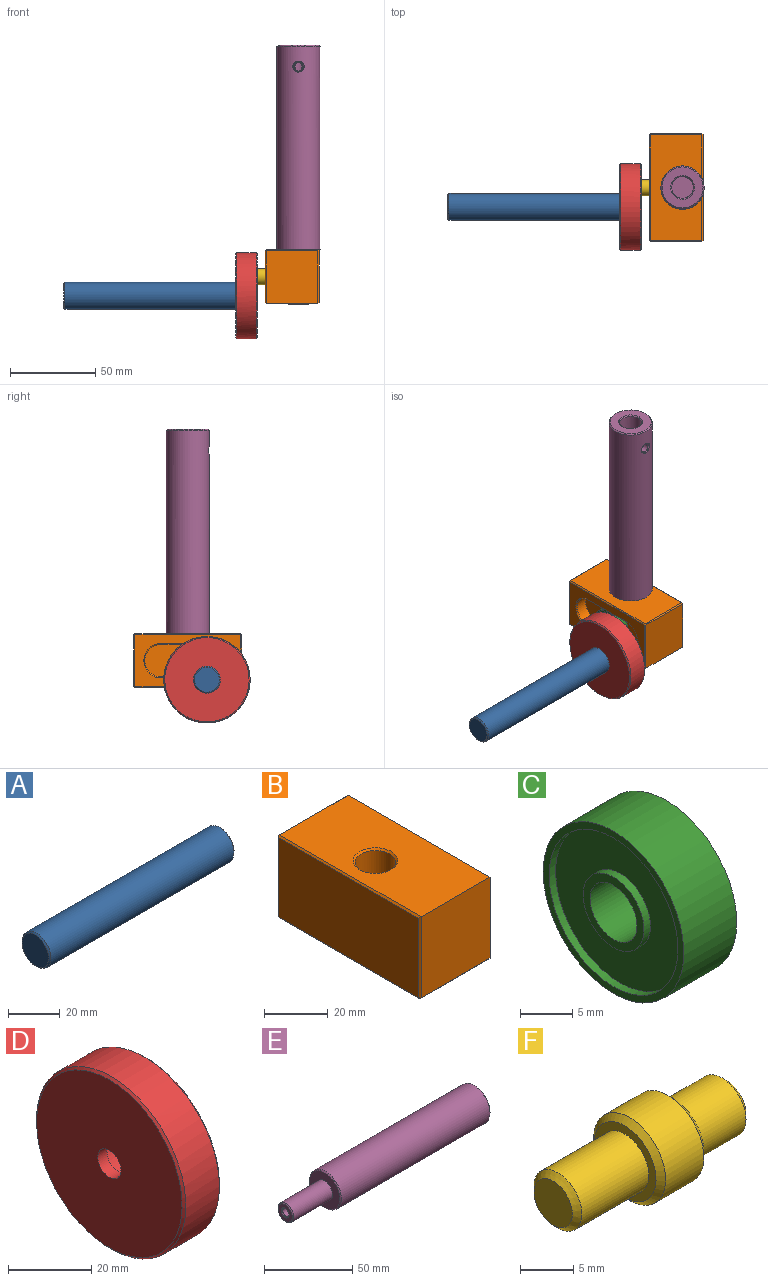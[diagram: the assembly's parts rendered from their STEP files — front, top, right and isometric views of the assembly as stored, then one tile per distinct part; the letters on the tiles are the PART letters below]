
ASSEMBLY  parts=6 mates=5
PART A: 8 faces, bbox 101.6x15.9x15.9 mm
  f0: plane 14.61x14.61mm, normal (-1,0,0), area 167.5mm2, adj f5
  f1: cylinder r=7.94mm len=100.33mm, axis (-1,0,0), area 5003.7mm2, adj f5,f6
  f2: plane 14.61x14.61mm, normal (1,0,0), area 135.6mm2, adj f6,f7
  f3: cone r=0mm half-angle=59deg, axis (1,0,0), area 23.9mm2, adj f4
  f4: cylinder r=2.55mm len=24.77mm, axis (1,0,0), area 397.2mm2, adj f3,f7
  f5: cone r=7.3mm half-angle=45deg, axis (1,0,0), area 43mm2, adj f0,f1
  f6: cone r=7.94mm half-angle=45deg, axis (-1,0,0), area 43mm2, adj f1,f2
  f7: cone r=2.55mm half-angle=45deg, axis (1,0,0), area 16.2mm2, adj f2,f4
PART B: 35 faces, bbox 31.8x63.5x31.8 mm
  f0: plane 62.23x30.48mm, normal (1,0,0), area 933.7mm2, adj f12,f13,f14,f15,f18,f20,f21,f22
  f1: plane 62.87x30.48mm, normal (0,0,1), area 1762.8mm2, adj f2,f17,f18,f23,f24
  f2: plane 31.12x30.48mm, normal (0,-1,0), area 948.4mm2, adj f1,f20,f28,f29
  f3: plane 62.23x30.48mm, normal (0,0,-1), area 1743.5mm2, adj f16,f21,f29,f30,f34
  f4: plane 30.48x30.48mm, normal (0,1,0), area 929mm2, adj f22,f23,f30,f31
  f5: plane 62.23x30.48mm, normal (-1,0,0), area 1896.8mm2, adj f24,f28,f31,f34
  f6: plane 31.75x6.99mm, normal (0,0,-1), area 221.8mm2, adj f7,f9,f10,f13
  f7: cylinder r=9.53mm len=19.05mm, axis (1,0,0), area 206.7mm2, adj f6,f8,f10,f15
  f8: plane 31.75x6.99mm, normal (0,0,1), area 221.8mm2, adj f7,f9,f10,f14
  f9: cylinder r=9.53mm len=19.05mm, axis (1,0,0), area 207mm2, adj f6,f8,f10,f12
  f10: plane 50.48x19.05mm, normal (1,0,0), area 883.9mm2, adj f6,f7,f8,f9
  f11: cylinder r=6.35mm len=30.48mm, axis (0,0,1), area 1216.1mm2, adj f16,f17
  f12: cone r=9.53mm half-angle=45deg, axis (1,0,0), area 27.5mm2, adj f0,f9,f13,f14
  f13: plane 31.76x0.64mm, normal (0.71,0,-0.71), area 28.5mm2, adj f0,f6,f12,f15
  f14: plane 31.76x0.64mm, normal (0.71,0,0.71), area 28.5mm2, adj f0,f8,f12,f15
  f15: cone r=9.53mm half-angle=45deg, axis (1,0,0), area 27.5mm2, adj f0,f7,f13,f14
  f16: cone r=6.99mm half-angle=45deg, axis (0,0,-1), area 37.6mm2, adj f3,f11
  f17: cone r=6.35mm half-angle=45deg, axis (0,0,1), area 37.6mm2, adj f1,f11
  f18: plane 62.87x0.64mm, normal (0.71,0,0.71), area 56.2mm2, adj f0,f1,f19,f20
  f19: plane 0.64x0.64mm, normal (0.58,0.58,0.58), area 0.3mm2, adj f18,f22,f23
  f20: plane 31.12x0.64mm, normal (0.71,-0.71,0), area 27.7mm2, adj f0,f2,f18,f25
  f21: plane 62.23x0.64mm, normal (0.71,0,-0.71), area 55.9mm2, adj f0,f3,f25,f26
  f22: plane 30.48x0.64mm, normal (0.71,0.71,0), area 27.4mm2, adj f0,f4,f19,f26
  f23: plane 30.48x0.64mm, normal (0,0.71,0.71), area 27.4mm2, adj f1,f4,f19,f27
  f24: plane 62.87x0.64mm, normal (-0.71,0,0.71), area 56.2mm2, adj f1,f5,f27,f28
  f25: plane 0.64x0.64mm, normal (0.58,-0.58,-0.58), area 0.3mm2, adj f20,f21,f29
  f26: plane 0.64x0.64mm, normal (0.58,0.58,-0.58), area 0.3mm2, adj f21,f22,f30
  f27: plane 0.64x0.64mm, normal (-0.58,0.58,0.58), area 0.3mm2, adj f23,f24,f31
  f28: plane 31.12x0.64mm, normal (-0.71,-0.71,0), area 27.7mm2, adj f2,f5,f24,f32
  f29: plane 30.48x0.64mm, normal (0,-0.71,-0.71), area 27.4mm2, adj f2,f3,f25,f32
  f30: plane 30.48x0.64mm, normal (0,0.71,-0.71), area 27.4mm2, adj f3,f4,f26,f33
  f31: plane 30.48x0.64mm, normal (-0.71,0.71,0), area 27.4mm2, adj f4,f5,f27,f33
  f32: plane 0.64x0.64mm, normal (-0.58,-0.58,-0.58), area 0.3mm2, adj f28,f29,f34
  f33: plane 0.64x0.64mm, normal (-0.58,0.58,-0.58), area 0.3mm2, adj f30,f31,f34
  f34: plane 62.23x0.64mm, normal (-0.71,0,-0.71), area 55.9mm2, adj f3,f5,f32,f33
PART C: 12 faces, bbox 7.2x19.1x19.1 mm
  f0: plane 8.26x8.26mm, normal (-1,0,0), area 21.9mm2, adj f5,f9
  f1: plane 8.26x8.26mm, normal (1,0,0), area 21.9mm2, adj f5,f6
  f2: plane 19.05x19.05mm, normal (1,0,0), area 54.2mm2, adj f3,f7
  f3: cylinder r=9.53mm len=19.05mm, axis (-1,0,0), area 429.4mm2, adj f2,f4
  f4: plane 19.05x19.05mm, normal (-1,0,0), area 45.5mm2, adj f3,f10
  f5: cylinder r=3.17mm len=7.18mm, axis (1,0,0), area 143.1mm2, adj f0,f1
  f6: cylinder r=4.13mm len=8.26mm, axis (1,0,0), area 23.1mm2, adj f1,f8
  f7: cylinder r=8.57mm len=17.15mm, axis (1,0,0), area 47.9mm2, adj f2,f8
  f8: plane 17.15x17.15mm, normal (1,0,0), area 177.3mm2, adj f6,f7
  f9: cylinder r=4.13mm len=8.26mm, axis (-1,0,0), area 23.1mm2, adj f0,f11
  f10: cylinder r=8.73mm len=17.46mm, axis (-1,0,0), area 48.8mm2, adj f4,f11
  f11: plane 17.46x17.46mm, normal (-1,0,0), area 186mm2, adj f9,f10
PART D: 10 faces, bbox 12.7x50.8x50.8 mm
  f0: cylinder r=25.4mm len=50.8mm, axis (-1,0,0), area 1824.1mm2, adj f8,f9
  f1: plane 49.53x49.53mm, normal (-1,0,0), area 1877.3mm2, adj f5,f8
  f2: plane 49.53x49.53mm, normal (1,0,0), area 1697.2mm2, adj f4,f7,f9
  f3: cone r=0mm half-angle=59deg, axis (1,0,0), area 36.9mm2, adj f4
  f4: cylinder r=3.17mm len=9.53mm, axis (1,0,0), area 190mm2, adj f2,f3
  f5: cylinder r=3.97mm len=7.94mm, axis (1,0,0), area 79.2mm2, adj f1,f6
  f6: plane 15.88x15.88mm, normal (1,0,0), area 148.4mm2, adj f5,f7
  f7: cylinder r=7.94mm len=15.88mm, axis (1,0,0), area 475mm2, adj f2,f6
  f8: cone r=24.77mm half-angle=45deg, axis (1,0,0), area 141.5mm2, adj f0,f1
  f9: cone r=25.4mm half-angle=45deg, axis (-1,0,0), area 141.5mm2, adj f0,f2
PART E: 18 faces, bbox 152.4x25.4x25.4 mm
  f0: cylinder r=12.7mm len=119.38mm, axis (1,0,0), area 9491.9mm2, adj f1,f9,f17
  f1: bspline ~6.7x6.43mm, area 14.5mm2, adj f0,f2
  f2: cylinder r=2.71mm len=5.41mm, axis (0,1,0), area 91.9mm2, adj f1,f3,f4,f5
  f3: cone r=0mm half-angle=59deg, axis (0,1,0), area 0mm2, adj f2,f5
  f4: cone r=0mm half-angle=59deg, axis (0,1,0), area 0mm2, adj f2,f5
  f5: cylinder r=6.35mm len=24.77mm, axis (1,0,0), area 970mm2, adj f2,f3,f4,f6,f8
  f6: cone r=6.35mm half-angle=45deg, axis (1,0,0), area 37.6mm2, adj f5,f7
  f7: plane 24.13x24.13mm, normal (1,0,0), area 304mm2, adj f6,f17
  f8: plane 12.7x12.7mm, normal (1,0,0), area 126.7mm2, adj f5
  f9: cone r=12.7mm half-angle=45deg, axis (1,0,0), area 69.9mm2, adj f0,f10
  f10: plane 24.13x24.13mm, normal (-1,0,0), area 330.6mm2, adj f9,f11
  f11: cylinder r=6.35mm len=31.12mm, axis (1,0,0), area 1241.4mm2, adj f10,f12
  f12: cone r=6.35mm half-angle=45deg, axis (1,0,0), area 34mm2, adj f11,f13
  f13: plane 11.43x11.43mm, normal (-1,0,0), area 70.7mm2, adj f12,f14
  f14: cone r=2.55mm half-angle=45deg, axis (-1,0,0), area 16.2mm2, adj f13,f15
  f15: cylinder r=2.55mm len=24.77mm, axis (-1,0,0), area 397.2mm2, adj f14,f16
  f16: cone r=0mm half-angle=59deg, axis (-1,0,0), area 23.9mm2, adj f15
  f17: cone r=12.06mm half-angle=45deg, axis (-1,0,0), area 69.9mm2, adj f0,f7
PART F: 11 faces, bbox 23.1x9.5x9.5 mm
  f0: plane 5.08x5.08mm, normal (1,0,0), area 20.3mm2, adj f10
  f1: cylinder r=3.17mm len=6.54mm, axis (-1,0,0), area 130.5mm2, adj f2,f10
  f2: plane 8.26x8.26mm, normal (1,0,0), area 21.9mm2, adj f1,f9
  f3: cylinder r=4.76mm len=9.53mm, axis (-1,0,0), area 152mm2, adj f8,f9
  f4: plane 8.26x8.26mm, normal (-1,0,0), area 21.9mm2, adj f5,f8
  f5: cylinder r=3.17mm len=8.89mm, axis (-1,0,0), area 177.3mm2, adj f4,f7
  f6: plane 5.08x5.08mm, normal (-1,0,0), area 20.3mm2, adj f7
  f7: cone r=2.54mm half-angle=45deg, axis (1,0,0), area 16.1mm2, adj f5,f6
  f8: cone r=4.13mm half-angle=45deg, axis (1,0,0), area 25.1mm2, adj f3,f4
  f9: cone r=4.76mm half-angle=45deg, axis (-1,0,0), area 25.1mm2, adj f2,f3
  f10: cone r=3.17mm half-angle=45deg, axis (-1,0,0), area 16.1mm2, adj f0,f1
PLACE A t=(-10.79,-165.11,-52.81)mm
PLACE B rot(axis=(0,1,0),180deg) t=(126.49,-71.35,-41.59)mm
PLACE C t=(9.94,30.26,-41.59)mm
PLACE D t=(-11.43,-82.56,-52.81)mm
PLACE E rot(axis=(0.71,0,0.71),180deg) t=(25.53,-223.75,18.42)mm
PLACE F t=(0.64,-20.54,-41.59)mm
MATE fastened D.f0 <-> A.f1  axis (-1,0,0) through (-11.43,-82.56,-52.81)mm
MATE fastened E.f0 <-> B.f11  axis (0,0,1) through (25.53,-71.35,-41.59)mm
MATE fastened D.f3 <-> F.f1  axis (1,0,0) through (-8.25,-71.34,-41.59)mm
MATE revolute F.f1 <-> C.f3  axis (1,0,0) through (13.53,-71.34,-41.59)mm
MATE slider B.f10 <-> C.f3  axis (-1,0,0) through (13.46,-71.34,-41.59)mm
